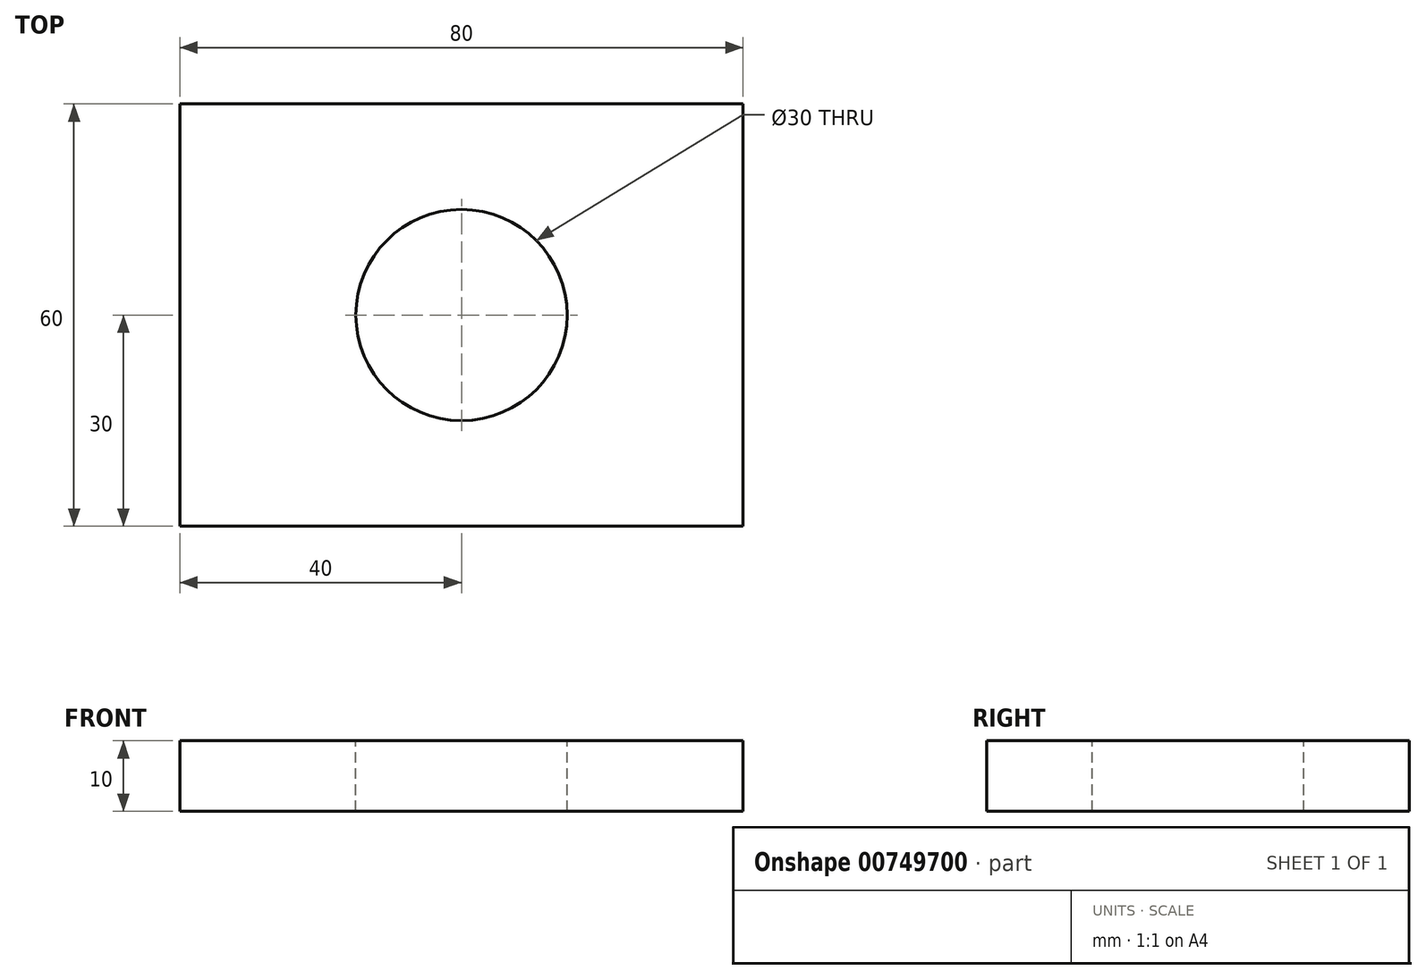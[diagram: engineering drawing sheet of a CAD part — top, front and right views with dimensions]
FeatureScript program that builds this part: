
annotation { "Feature Type Name" : "Feature", "Feature Type Description" : "" }
export const myFeature = defineFeature(function(context is Context, id is Id, definition is map)
    precondition{}
    {
        {
            var Q0;
            Q0=qCreatedBy(makeId("Top.planeOp"),FACE);
            var sketch = newSketch(context, id + "F0", { "sketchPlane" : qUnion([Q0])});
            skLineSegment(sketch, "E0.bottom", {"start": v(0, 0) * mm, "end": v(80, 0) * mm});
            skLineSegment(sketch, "E0.top", {"start": v(0, 60) * mm, "end": v(80, 60) * mm});
            skLineSegment(sketch, "E0.left", {"start": v(0, 0) * mm, "end": v(0, 60) * mm});
            skLineSegment(sketch, "E0.right", {"start": v(80, 0) * mm, "end": v(80, 60) * mm});
            skSolve(sketch);
        }
        {
            var Q0;
            Q0 = qSketchRegion(id + "F0", true);
            var Q1;
            Q1=makeQuery(id+"F0.imprint","IMPRINT",FACE,{"disambiguationData":[TD([[makeQuery(id+"F0.imprint","IMPRINT",EDGE,{"derivedFrom":sQuery(id+"F0.wireOp",EDGE,"E0.bottom")}),1.0]])]});
            extrude(context, id + "F1", {"entities" : qUnion([Q0, Q1]), "depth" : 10 * mm, "offsetDistance" : 25 * mm});
        }
        {
            var Q0;
            Q0=makeQuery(id+"F1.opExtrude","CAP_FACE",FACE,{"disambiguationData":[OSD([sQuery(id+"F0.wireOp",EDGE,"E0.bottom"),sQuery(id+"F0.wireOp",EDGE,"E0.top"),sQuery(id+"F0.wireOp",EDGE,"E0.left"),sQuery(id+"F0.wireOp",EDGE,"E0.right")])],"isStart":false});
            var sketch = newSketch(context, id + "F2", { "sketchPlane" : qUnion([Q0])});
            skLineSegment(sketch, "E1", {"start": v(40, 60) * mm, "end": v(40, 30) * mm});
            skCircle(sketch, "E2", {"center": v(40, 30) * mm, "radius": 15 * mm});
            skSolve(sketch);
        }
        {
            var Q0;
            Q0 = qSketchRegion(id + "F2", true);
            var Q1;
            Q1=makeQuery(id+"F2.imprint","IMPRINT",FACE,{"disambiguationData":[TD([[makeQuery(id+"F2.imprint","IMPRINT",EDGE,{"derivedFrom":sQuery(id+"F2.wireOp",EDGE,"E2")}),1.0]])]});
            extrude(context, id + "F3", {"entities" : qUnion([Q0, Q1]), "operationType" : NewBodyOperationType.REMOVE, "endBound" : BoundingType.THROUGH_ALL, "oppositeDirection" : true, "depth" : 25 * mm, "offsetDistance" : 25 * mm});
        }
    });
